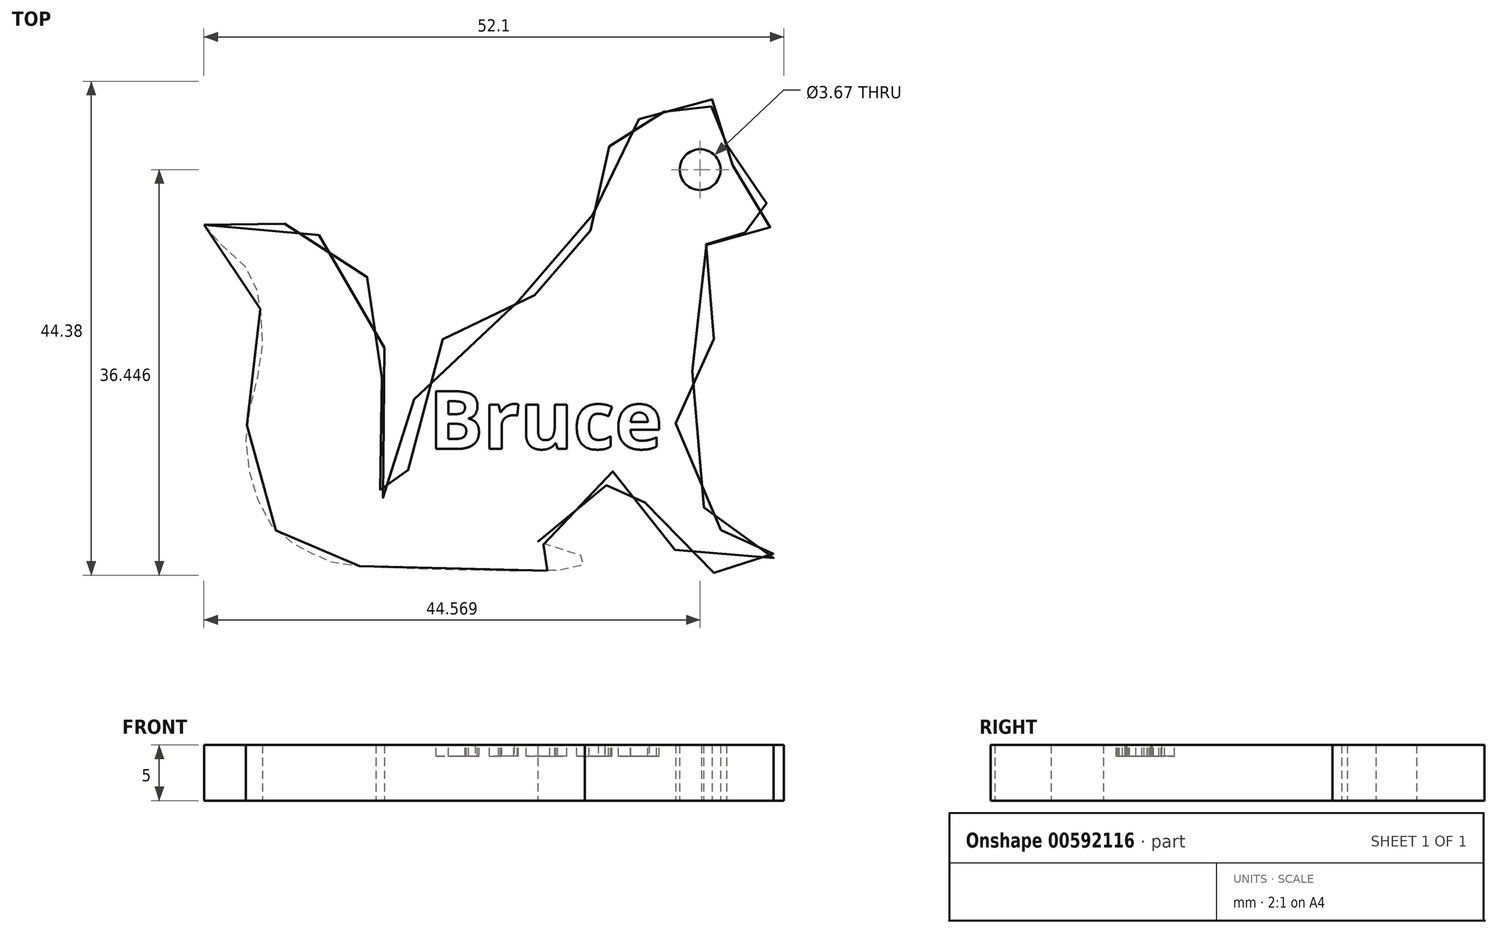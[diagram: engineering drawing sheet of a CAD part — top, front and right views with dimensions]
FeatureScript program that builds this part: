
annotation { "Feature Type Name" : "Feature", "Feature Type Description" : "" }
export const myFeature = defineFeature(function(context is Context, id is Id, definition is map)
    precondition{}
    {
        {
            var Q0;
            Q0=qCreatedBy(makeId("Top.planeOp"),FACE);
            var sketch = newSketch(context, id + "F0", { "sketchPlane" : qUnion([Q0])});
            skFitSpline(sketch, "E0", {"points": [v(-55.47, 37.81) * mm, v(-51.98, 34.32) * mm, v(-50.5, 30.82) * mm, v(-50.32, 26.04) * mm, v(-51.61, 19.96) * mm, v(-51.24, 15) * mm, v(-49.03, 10.4) * mm, v(-45.9, 8.37) * mm, v(-43.7, 7.45) * mm, v(-34.5, 6.9) * mm, v(-21.8, 7.08) * mm, v(-21.25, 7.64) * mm, v(-22.17, 8.37) * mm, v(-25.48, 9.3) * mm, v(-21.44, 11.13) * mm, v(-18.12, 16.47) * mm, v(-15.73, 12.6) * mm, v(-10.76, 6.9) * mm, v(-5.06, 6.9) * mm, v(-4.32, 8.19) * mm, v(-5.61, 9.3) * mm, v(-8.37, 9.84) * mm, v(-12.97, 18.68) * mm, v(-11.68, 24.56) * mm, v(-8.56, 31.37) * mm, v(-10.58, 37.26) * mm, v(-8.74, 37.81) * mm, v(-5.98, 37.08) * mm, v(-3.4, 39.1) * mm, v(-7.45, 40.75) * mm, v(-8.37, 44.8) * mm, v(-10.76, 46.1) * mm, v(-10.21, 47.2) * mm, v(-10.4, 50.7) * mm, v(-14.81, 47.56) * mm, v(-16.84, 47.2) * mm, v(-19.96, 42.96) * mm, v(-20.7, 37.63) * mm, v(-23.46, 32.84) * mm, v(-30.08, 29.9) * mm, v(-36.16, 24.01) * mm, v(-37.81, 11.87) * mm, v(-39.47, 13.52) * mm, v(-39.65, 22.54) * mm, v(-39.83, 31.19) * mm, v(-44.8, 36.7) * mm, v(-51.98, 38.36) * mm, v(-55.47, 37.81) * mm]});
            skCircle(sketch, "E1", {"center": v(-10.91, 42.78) * mm, "radius": 1.83 * mm});
            skSolve(sketch);
        }
        {
            var Q0;
            Q0=makeQuery(id+"F0.imprint","IMPRINT",FACE,{"disambiguationData":[TD([[makeQuery(id+"F0.imprint","IMPRINT",EDGE,{"derivedFrom":sQuery(id+"F0.wireOp",EDGE,"E0")}),1.0]])]});
            extrude(context, id + "F1", {"entities" : qUnion([Q0]), "depth" : 5 * mm, "offsetDistance" : 25 * mm});
        }
        {
            var Q0;
            Q0 = qSketchRegion(id + "F0", true);
            extrude(context, id + "F2", {"entities" : qUnion([Q0]), "operationType" : NewBodyOperationType.ADD, "depth" : 5 * mm, "offsetDistance" : 25 * mm});
        }
        {
            var Q0;
            Q0=makeQuery(id+"F1.opExtrude","CAP_FACE",FACE,{"disambiguationData":[OSD([sQuery(id+"F0.wireOp",EDGE,"E0"),sQuery(id+"F0.wireOp",EDGE,"E1")])],"isStart":false});
            var sketch = newSketch(context, id + "F3", { "sketchPlane" : qUnion([Q0])});
            skText(sketch, "E2", { "text": "Bruce", "fontName": "OpenSans-Bold.ttf"});
            const initialGuessF3  = {"E2": [-0.03527, 0.01768, 1, 0, 0.00523]};
            skSetInitialGuess(sketch, initialGuessF3);
            skSolve(sketch);
        }
        {
            var Q0;
            Q0 = qSketchRegion(id + "F3", true);
            extrude(context, id + "F4", {"entities" : qUnion([Q0]), "operationType" : NewBodyOperationType.REMOVE, "oppositeDirection" : true, "depth" : mm, "offsetDistance" : 25 * mm});
        }
        {
            var Q0;
            Q0 = qSketchRegion(id + "F3", true);
            extrude(context, id + "F5", {"entities" : qUnion([Q0]), "operationType" : NewBodyOperationType.REMOVE, "oppositeDirection" : true, "depth" : 1 * mm, "offsetDistance" : 25 * mm});
        }
    });
